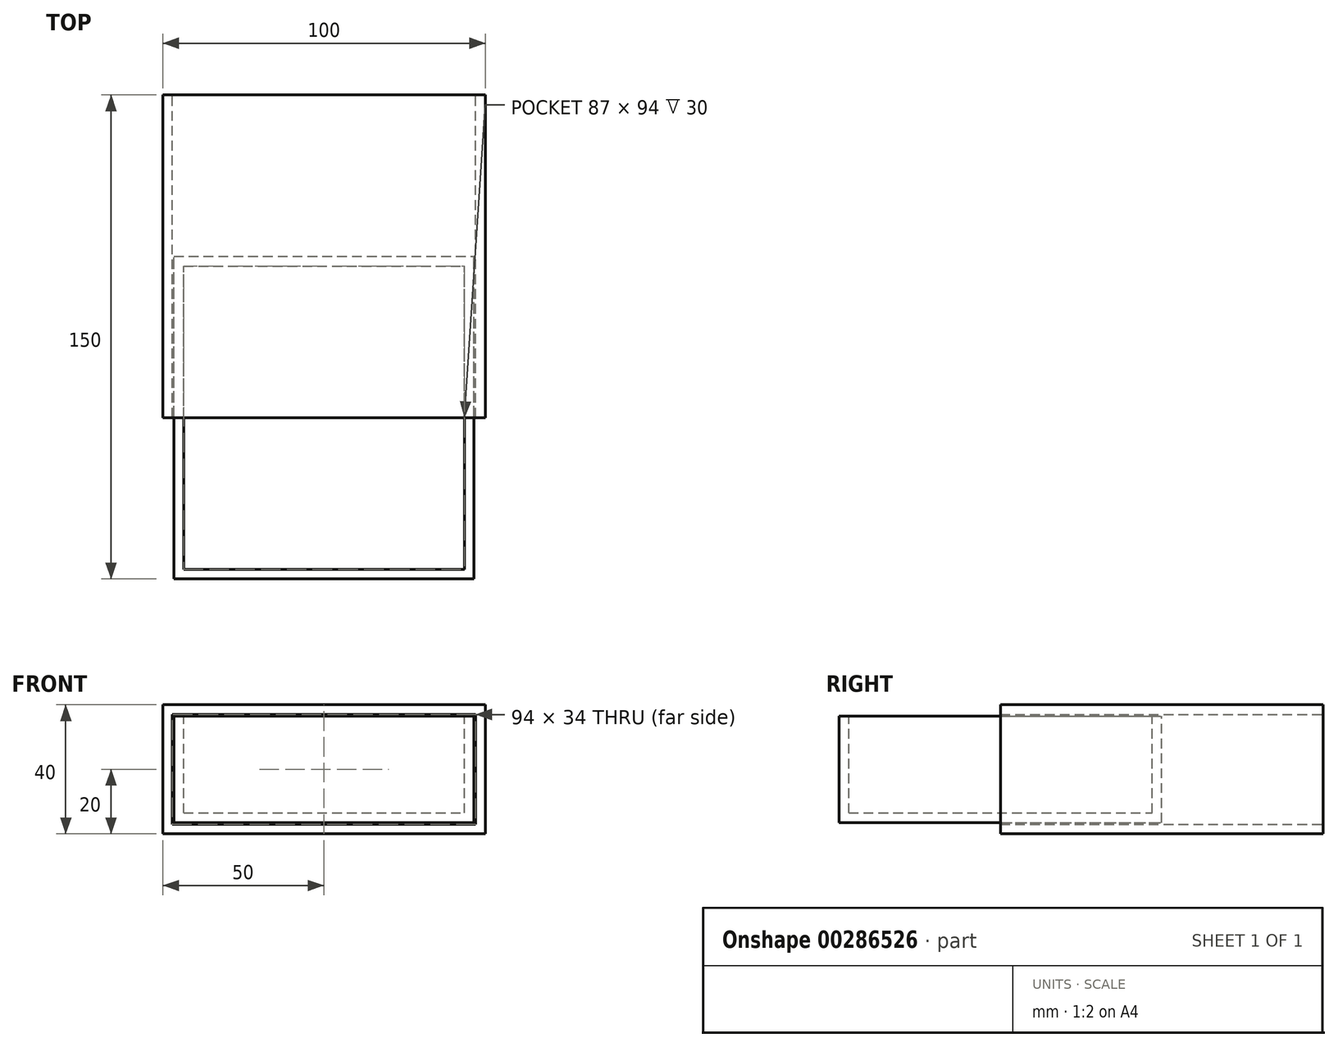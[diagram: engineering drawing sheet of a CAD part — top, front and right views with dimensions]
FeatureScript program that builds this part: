
annotation { "Feature Type Name" : "Feature", "Feature Type Description" : "" }
export const myFeature = defineFeature(function(context is Context, id is Id, definition is map)
    precondition{}
    {
        {
            var Q0;
            Q0=qCreatedBy(makeId("Front.planeOp"),FACE);
            var sketch = newSketch(context, id + "F0", { "sketchPlane" : qUnion([Q0])});
            skLineSegment(sketch, "E0.bottom", {"start": v(0, 0) * mm, "end": v(100, 0) * mm});
            skLineSegment(sketch, "E0.top", {"start": v(0, 40) * mm, "end": v(100, 40) * mm});
            skLineSegment(sketch, "E0.left", {"start": v(0, 0) * mm, "end": v(0, 40) * mm});
            skLineSegment(sketch, "E0.right", {"start": v(100, 0) * mm, "end": v(100, 40) * mm});
            skLineSegment(sketch, "E1.0", {"start": v(3, 3) * mm, "end": v(3, 37) * mm});
            skLineSegment(sketch, "E1.1", {"start": v(3, 3) * mm, "end": v(97, 3) * mm});
            skLineSegment(sketch, "E1.2", {"start": v(97, 3) * mm, "end": v(97, 37) * mm});
            skLineSegment(sketch, "E1.3", {"start": v(3, 37) * mm, "end": v(97, 37) * mm});
            skSolve(sketch);
        }
        {
            var Q0;
            Q0 = qSketchRegion(id + "F0", true);
            extrude(context, id + "F1", {"entities" : qUnion([Q0]), "depth" : 100 * mm, "offsetDistance" : 25 * mm});
        }
        {
            var Q0;
            Q0=makeQuery(id+"F1.opExtrude","CAP_FACE",FACE,{"disambiguationData":[OSD([sQuery(id+"F0.wireOp",EDGE,"E0.bottom"),sQuery(id+"F0.wireOp",EDGE,"E0.top"),sQuery(id+"F0.wireOp",EDGE,"E0.left"),sQuery(id+"F0.wireOp",EDGE,"E0.right"),sQuery(id+"F0.wireOp",EDGE,"E1.0"),sQuery(id+"F0.wireOp",EDGE,"E1.1"),sQuery(id+"F0.wireOp",EDGE,"E1.2"),sQuery(id+"F0.wireOp",EDGE,"E1.3")])],"isStart":false});
            var sketch = newSketch(context, id + "F2", { "sketchPlane" : qUnion([Q0])});
            skLineSegment(sketch, "E2.0", {"start": v(3.5, 36.5) * mm, "end": v(96.5, 36.5) * mm});
            skLineSegment(sketch, "E2.1", {"start": v(3.5, 3.5) * mm, "end": v(3.5, 36.5) * mm});
            skLineSegment(sketch, "E2.2", {"start": v(3.5, 3.5) * mm, "end": v(96.5, 3.5) * mm});
            skLineSegment(sketch, "E2.3", {"start": v(96.5, 3.5) * mm, "end": v(96.5, 36.5) * mm});
            skSolve(sketch);
        }
        {
            var Q0;
            Q0 = qSketchRegion(id + "F2", true);
            extrude(context, id + "F3", {"entities" : qUnion([Q0]), "depth" : 100 * mm, "offsetDistance" : 25 * mm, "symmetric" : true});
        }
        {
            var Q0;
            Q0=makeQuery(id+"F3.opExtrude","SWEPT_FACE",FACE,{"disambiguationData":[OSD([sQuery(id+"F2.wireOp",EDGE,"E2.0")])]});
            shell(context, id + "F4", {"entities" : qUnion([Q0]), "thickness" : 3 * mm});
        }
    });
